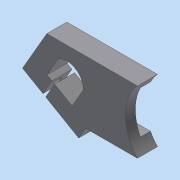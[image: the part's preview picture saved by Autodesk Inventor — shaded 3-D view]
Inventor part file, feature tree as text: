
AUTODESK INVENTOR PART (.ipt)
format: ipt  version: 2017 (Build 210142000, 142)  size: 147,456 bytes
history: native  units: in
note: dims shown in document units (in); Inventor stores cm internally (conversion verified against a paired STEP export)
features: extrude x5, plane x1, sketch x1
ambient origin geometry x8: Origin, YZ Plane, XZ Plane, XY Plane, X Axis, Y Axis, Z Axis, Center Point
bodies: Solid1 (feature_tree)
feature tree (7):
  extrude  "plate"  Depth=0.45in
  extrude  "cut out"  Depth=0.72in
  extrude  "tension holes"  Depth=0.45in
  plane  "Work Plane1"
  sketch  "Sketch2"  dims[d2=2.3228in d3=0.56in d4=0.72in d11=0.45in d20=0.7874in d22=0.5in d23=0.7874in d25=0.75in d45=0.125in d46=0.25in d47=0.0in d48=0.0787in d49=0.5in d50=0.0in d54=0.2in d55=0.0in d56=0.41in d57=1.06in d58=0.45in d59=30.0deg d60=0.1875in d63=-1.2in d67=1.0in d68=0.0in d69=0.816in d83=1.0in d84=0.0in d88=0.25in d89=0.25in d90=0.45in d91=0.313in d92=0.3287in d93=0.36in d94=0.159in]
  extrude  "clamp screw"  Depth=0.5in
  extrude  "clamp nut"  Depth=0.125in
